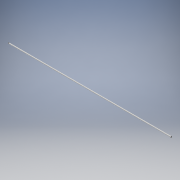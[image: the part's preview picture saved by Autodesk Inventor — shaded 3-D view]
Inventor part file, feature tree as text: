
AUTODESK INVENTOR PART (.ipt)
format: ipt  version: 2017 (Build 210142000, 142)  size: 91,648 bytes
history: native  units: mm
features: extrude x1, sketch x1
ambient origin geometry x8: Origin, YZ Plane, XZ Plane, XY Plane, X Axis, Y Axis, Z Axis, Center Point
bodies: Solid1 (feature_tree)
feature tree (2):
  extrude  "Extrusion1"  Depth=4000.0mm
  sketch  "Sketch1"  dims[d0=26.0mm d1=2.7mm d2=4000.0mm d3=0.0mm]
